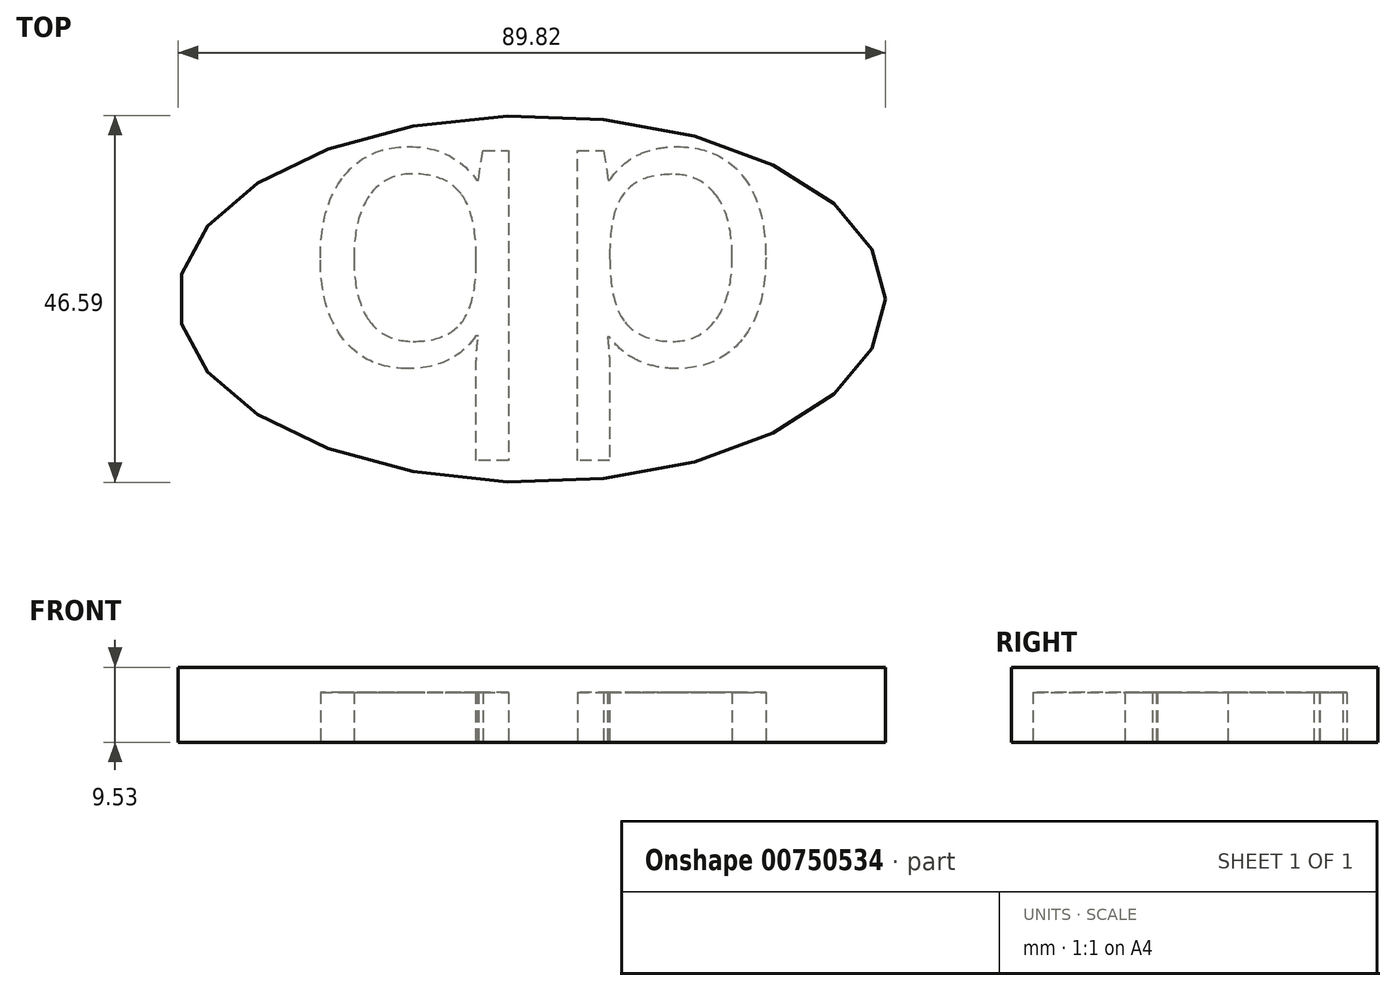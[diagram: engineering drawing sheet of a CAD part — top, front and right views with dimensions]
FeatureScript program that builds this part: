
annotation { "Feature Type Name" : "Feature", "Feature Type Description" : "" }
export const myFeature = defineFeature(function(context is Context, id is Id, definition is map)
    precondition{}
    {
        {
            var Q0;
            Q0=qCreatedBy(makeId("Top.planeOp"),FACE);
            var sketch = newSketch(context, id + "F0", { "sketchPlane" : qUnion([Q0])});
            skLineSegment(sketch, "E0.bottom", {"start": v(-33.28, 38.07) * mm, "end": v(61.97, 38.07) * mm});
            skLineSegment(sketch, "E0.top", {"start": v(-33.28, -31.78) * mm, "end": v(61.97, -31.78) * mm});
            skLineSegment(sketch, "E0.left", {"start": v(-33.28, 38.07) * mm, "end": v(-33.28, -31.78) * mm});
            skLineSegment(sketch, "E0.right", {"start": v(61.97, 38.07) * mm, "end": v(61.97, -31.78) * mm});
            skSolve(sketch);
        }
        {
            var Q0;
            Q0=makeQuery(id+"F0.imprint","IMPRINT",FACE,{"disambiguationData":[TD([[makeQuery(id+"F0.imprint","IMPRINT",EDGE,{"derivedFrom":sQuery(id+"F0.wireOp",EDGE,"E0.bottom")}),-1.0]])]});
            extrude(context, id + "F1", {"entities" : qUnion([Q0]), "depth" : 9.52 * mm, "offsetDistance" : 25.4 * mm});
        }
        {
            var Q0;
            Q0=qCreatedBy(makeId("Top.planeOp"),FACE);
            var sketch = newSketch(context, id + "F2", { "sketchPlane" : qUnion([Q0])});
            skText(sketch, "E1", { "text": "qp", "fontName": "OpenSans-Regular.ttf"});
            const initialGuessF2  = {"E1": [-0.01755, -0.01657, 1, 0, 0.03657]};
            skSetInitialGuess(sketch, initialGuessF2);
            skSolve(sketch);
        }
        {
            var Q0;
            Q0=qSketchRegion(id+"F2",true);
            extrude(context, id + "F3", {"entities" : qUnion([Q0]), "operationType" : NewBodyOperationType.REMOVE, "depth" : 6.35 * mm, "offsetDistance" : 25.4 * mm});
        }
        {
            var Q0;
            {var subQ0=sQuery(id+"F0.wireOp",EDGE,"E0.left");var subQ1=sQuery(id+"F0.wireOp",EDGE,"E0.top");var subQ2=sQuery(id+"F0.wireOp",EDGE,"E0.right");var subQ3=sQuery(id+"F0.wireOp",EDGE,"E0.bottom");Q0=makeQuery(id+"F3.boolean.opBoolean","SPLIT",FACE,{"disambiguationData":[TD([makeQuery(id+"F1.opExtrude","SWEPT_FACE",FACE,{"disambiguationData":[OSD([subQ3])]})])],"derivedFrom":makeQuery(id+"F1.opExtrude","CAP_FACE",FACE,{"disambiguationData":[OSD([subQ3,subQ1,subQ0,subQ2])],"isStart":true})});}
            var sketch = newSketch(context, id + "F4", { "sketchPlane" : qUnion([Q0])});
            skPoint(sketch, "E2.center.orphan", {"position": v(12.4, 0) * mm});
            skEllipse(sketch, "E3", {"center": v(12.15, 8.22) * mm, "majorRadius": 44.91 * mm, "minorRadius": 23.3 * mm, "majorAxis": v(1, 0)});
            skLineSegment(sketch, "E4.bottom", {"start": v(-33.28, 31.78) * mm, "end": v(61.97, 31.78) * mm});
            skLineSegment(sketch, "E4.top", {"start": v(-33.28, -38.07) * mm, "end": v(61.97, -38.07) * mm});
            skLineSegment(sketch, "E4.left", {"start": v(-33.28, 31.78) * mm, "end": v(-33.28, -38.07) * mm});
            skLineSegment(sketch, "E4.right", {"start": v(61.97, 31.78) * mm, "end": v(61.97, -38.07) * mm});
            skSolve(sketch);
        }
        {
            var Q0;
            Q0=makeQuery(id+"F4.imprint","IMPRINT",FACE,{"disambiguationData":[TD([[makeQuery(id+"F4.imprint","IMPRINT",EDGE,{"derivedFrom":sQuery(id+"F4.wireOp",EDGE,"E3")}),-1.0]])]});
            extrude(context, id + "F5", {"entities" : qUnion([Q0]), "operationType" : NewBodyOperationType.REMOVE, "oppositeDirection" : true, "depth" : 25.4 * mm, "offsetDistance" : 25.4 * mm});
        }
    });
